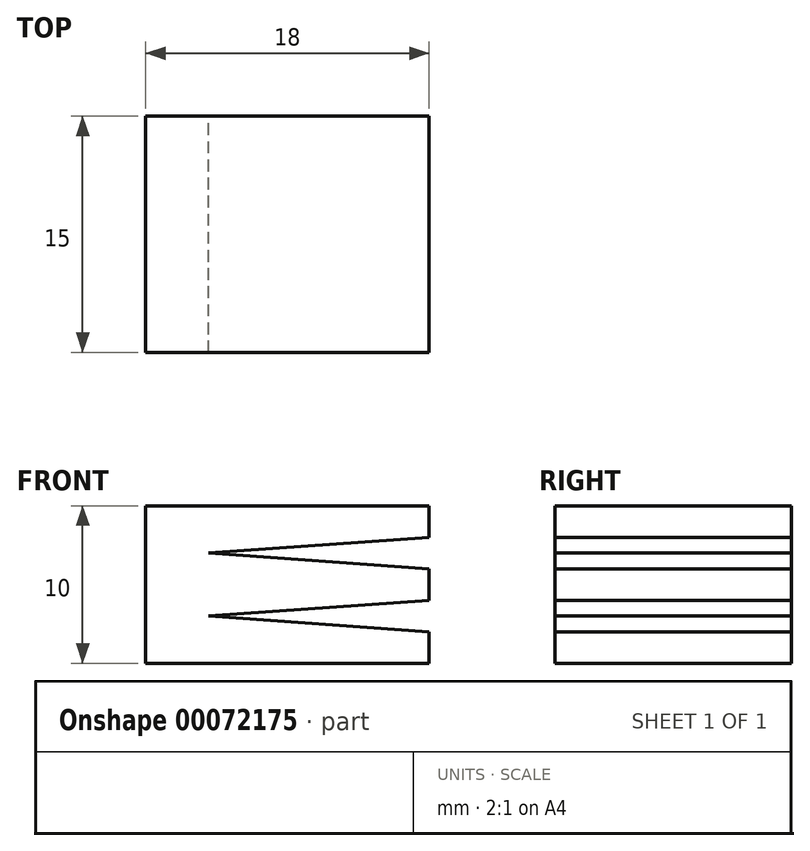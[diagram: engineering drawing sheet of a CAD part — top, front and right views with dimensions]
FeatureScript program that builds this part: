
annotation { "Feature Type Name" : "Feature", "Feature Type Description" : "" }
export const myFeature = defineFeature(function(context is Context, id is Id, definition is map)
    precondition{}
    {
        {
            var Q0;
            Q0=qCreatedBy(makeId("Front.planeOp"),FACE);
            var sketch = newSketch(context, id + "F0", { "sketchPlane" : qUnion([Q0])});
            skLineSegment(sketch, "E0.rect.bottom", {"start": v(9, 5) * mm, "end": v(-9, 5) * mm});
            skLineSegment(sketch, "E0.rect.top", {"start": v(9, -5) * mm, "end": v(-9, -5) * mm});
            skLineSegment(sketch, "E0.rect.left", {"start": v(9, 5) * mm, "end": v(9, 3) * mm});
            skLineSegment(sketch, "E0.rect.right", {"start": v(-9, 5) * mm, "end": v(-9, -5) * mm});
            skPoint(sketch, "E0.rect.middle", {"position": v(0, 0) * mm});
            skPoint(sketch, "E1", {"position": v(9, 3) * mm});
            skPoint(sketch, "E2", {"position": v(9, 1) * mm});
            skPoint(sketch, "E3", {"position": v(9, -1) * mm});
            skPoint(sketch, "E4", {"position": v(9, -3) * mm});
            skLineSegment(sketch, "E5", {"start": v(-5, 2) * mm, "end": v(9, 3) * mm});
            skLineSegment(sketch, "E6", {"start": v(-5, 2) * mm, "end": v(9, 1) * mm});
            skLineSegment(sketch, "E7", {"start": v(-5, -2) * mm, "end": v(9, -1) * mm});
            skLineSegment(sketch, "E8", {"start": v(-5, -2) * mm, "end": v(9, -3) * mm});
            skLineSegment(sketch, "E9.trimOffspring", {"start": v(9, 1) * mm, "end": v(9, -1) * mm});
            skLineSegment(sketch, "E10.trimOffspring", {"start": v(9, -3) * mm, "end": v(9, -5) * mm});
            skSolve(sketch);
        }
        {
            var Q0;
            Q0=makeQuery(id+"F0.imprint","IMPRINT",FACE,{"disambiguationData":[TD([[makeQuery(id+"F0.imprint","IMPRINT",EDGE,{"derivedFrom":sQuery(id+"F0.wireOp",EDGE,"E0.rect.bottom")}),1.0]])]});
            extrude(context, id + "F1", {"entities" : qUnion([Q0]), "depth" : 15 * mm});
        }
    });
